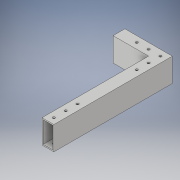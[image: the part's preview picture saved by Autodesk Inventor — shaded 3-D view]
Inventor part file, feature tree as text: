
AUTODESK INVENTOR PART (.ipt)
format: ipt  version: 2018 (Build 220112000, 112)  size: 179,200 bytes
history: native  units: in
note: dims shown in document units (in); Inventor stores cm internally (conversion verified against a paired STEP export)
features: extrude x5, sketch x5
ambient origin geometry x8: Origin, YZ Plane, XZ Plane, XY Plane, X Axis, Y Axis, Z Axis, Center Point
bodies: Body1 (feature_tree)
feature tree (10):
  extrude  "Extrusion12"  Depth=2.0in
  extrude  "Extrusion13"  Depth=0.1in
  extrude  "Extrusion14"  Depth=0.1in
  extrude  "Extrusion16"  Depth=1.0in
  extrude  "Extrusion17"  Depth=0.1in
  sketch  "Sketch15"  dims[d46=1.0in d47=2.0in]
  sketch  "Sketch16"  dims[d48=0.1in d49=0.1in]
  sketch  "Sketch17"  dims[d50=0.1in d51=0.1in]
  sketch  "Sketch20"  dims[d52=3.0in d53=0.0in d54=1.0in]
  sketch  "Sketch21"  dims[d55=2.0in d56=0.1in d57=0.1in d58=0.1in d59=0.1in d60=10.0in d61=0.0in d62=0.1in d63=0.0in d71=0.5in d72=0.5in d73=0.5in d74=0.2031in d75=0.2031in d76=0.2031in d77=0.5in d78=0.5in d79=0.2031in d80=0.2031in d81=0.5in d82=1.0in d83=1.0in d84=1.0in d85=1.0in d86=3.0in d87=0.0in d88=0.2031in d89=0.2031in d90=0.2031in d91=1.0in d92=1.0in d93=0.5in d94=0.5in d95=0.5in d96=0.5in d97=3.0in d98=0.0in]
